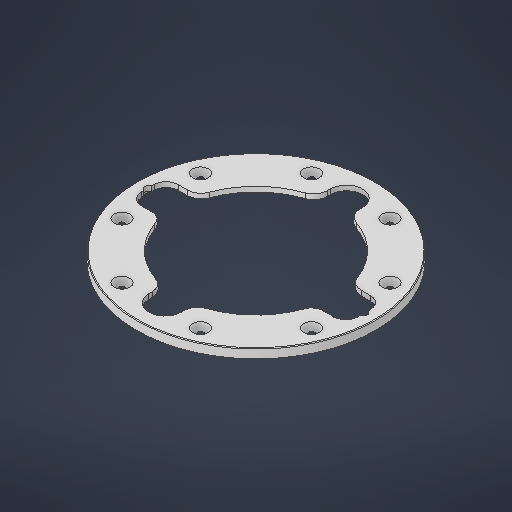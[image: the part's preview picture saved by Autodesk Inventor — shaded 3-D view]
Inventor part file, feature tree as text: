
AUTODESK INVENTOR PART (.ipt)
format: ipt  version: 2025 (Build 290162000, 162)  size: 321,536 bytes
history: native  units: in
note: dims shown in document units (in); Inventor stores cm internally (conversion verified against a paired STEP export)
features: sketch x5, extrude x3, hole x3, chamfer x1
ambient origin geometry x8: Origin, YZ Plane, XZ Plane, XY Plane, X Axis, Y Axis, Z Axis, Center Point
bodies: Solid1 (feature_tree)
feature tree (12):
  sketch  "Sketch1"  dims[d2=4.3701in d10=0.2559in d11=0.0in]
  extrude  "Extrusion1"  Depth=0.2559in TaperAngle=0.0deg
  extrude  "Extrusion2"  Depth=0.1378in
  sketch  "Sketch2"  dims[d12=0.1378in d13=0.0in d14=5.7087in]
  hole  "Hole1"  [1 undecoded]
  chamfer  "Chamfer2"  Distance=0.3937in
  hole  "Hole2"  [1 undecoded]
  extrude  "Extrusion4"  Depth=0.3937in
  hole  "Hole4"  [1 undecoded]
  sketch  "Sketch4"  dims[d27=0.1378in d28=0.2362in d29=0.1575in d30=0.0787in d31=90.0deg d32=0.3465in d33=0.0in d34=0.0197in d35=0.0787in d36=45.0deg]
  sketch  "Sketch Circular Pattern3"  dims[d15=0.0787in]
  sketch  "Sketch5"  dims[d37=0.1628in d38=0.3937in d39=0.4409in d40=0.0787in d41=90.0deg d42=0.5591in d43=0.0in d60=4.4094in d74=0.3937in d75=0.0in d76=4.3307in d77=90.0deg d78=0.315in d79=0.9843in d80=2.9921in d81=0.3937in d82=2.5236in d83=0.3937in d84=0.4291in d85=0.0197in d86=0.315in d87=22.5deg d88=0.1969in d89=3.1496in d91=360.0deg d93=0.1969in d94=0.1969in d95=0.2165in d96=0.3937in d97=0.4409in d98=0.0787in d99=90.0deg d100=0.5591in d101=0.0in d102=5.9843in]
note: 3 required parameter values undecoded (feature->parameter linkage not recoverable at this tier; creation-order binding heuristic only, values carry confidence <= 0.55)
